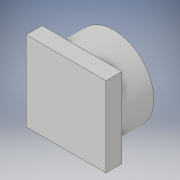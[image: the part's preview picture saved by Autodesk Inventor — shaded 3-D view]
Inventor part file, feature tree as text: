
AUTODESK INVENTOR PART (.ipt)
format: ipt  version: 2018 (Build 220112000, 112)  size: 103,424 bytes
history: native  units: mm
features: extrude x2, sketch x2
ambient origin geometry x8: Origin, YZ Plane, XZ Plane, XY Plane, X Axis, Y Axis, Z Axis, Center Point
bodies: Volumenkörper1 (feature_tree)
feature tree (4):
  extrude  "Extrusion1"  Depth=20.0mm TaperAngle=0.0deg
  extrude  "Extrusion2"  [1 undecoded]
  sketch  "Skizze1"  dims[d0=50.0mm d1=20.0mm d2=0.0mm]
  sketch  "Skizze2"  dims[d3=10.0mm d4=0.0mm]
note: 1 required parameter value undecoded (feature->parameter linkage not recoverable at this tier; creation-order binding heuristic only, values carry confidence <= 0.55)
